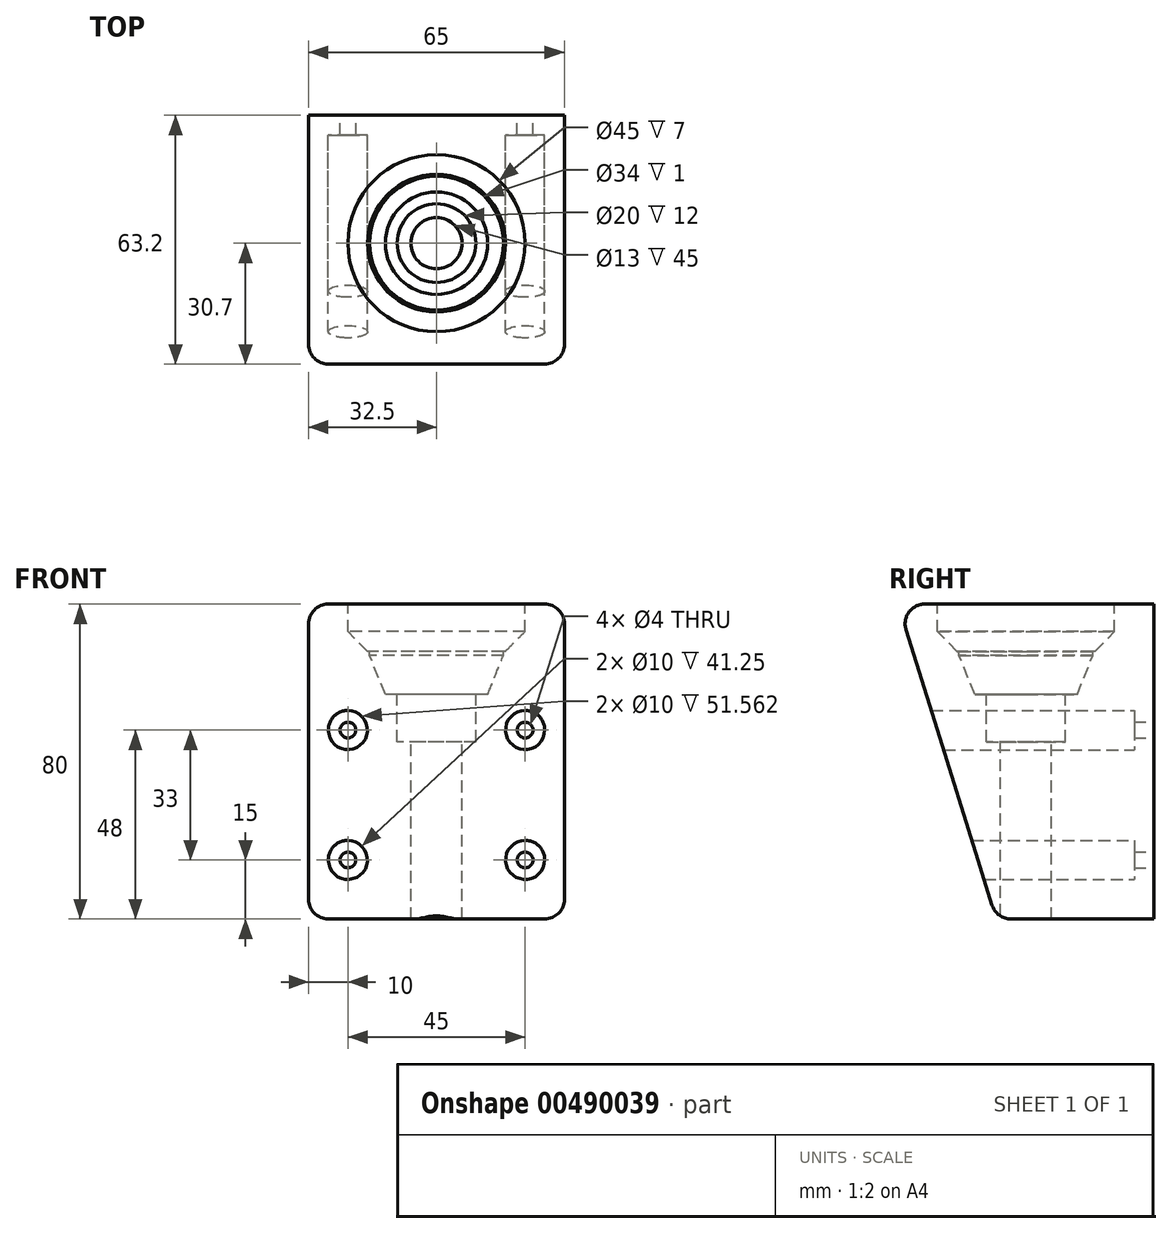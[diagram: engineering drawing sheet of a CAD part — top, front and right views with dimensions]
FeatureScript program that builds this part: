
annotation { "Feature Type Name" : "Feature", "Feature Type Description" : "" }
export const myFeature = defineFeature(function(context is Context, id is Id, definition is map)
    precondition{}
    {
        {
            var Q0;
            Q0=qCreatedBy(makeId("Right.planeOp"),FACE);
            var sketch = newSketch(context, id + "F0", { "sketchPlane" : qUnion([Q0])});
            skLineSegment(sketch, "E0", {"start": v(0, 0) * mm, "end": v(0, 80) * mm});
            skLineSegment(sketch, "E1", {"start": v(0, 80) * mm, "end": v(-65, 80) * mm});
            skLineSegment(sketch, "E2", {"start": v(0, 0) * mm, "end": v(-40, 0) * mm});
            skLineSegment(sketch, "E3", {"start": v(-40, 0) * mm, "end": v(-65, 80) * mm});
            skSolve(sketch);
        }
        {
            var Q0;
            Q0=makeQuery(id+"F0.imprint","IMPRINT",FACE,{"disambiguationData":[TD([[makeQuery(id+"F0.imprint","IMPRINT",EDGE,{"derivedFrom":sQuery(id+"F0.wireOp",EDGE,"E0")}),1.0]])]});
            extrude(context, id + "F1", {"entities" : qUnion([Q0]), "endBound" : BoundingType.SYMMETRIC, "depth" : 65 * mm});
        }
        {
            var Q0;
            Q0=makeQuery(id+"F1.opExtrude","SWEPT_FACE",FACE,{"disambiguationData":[OSD([sQuery(id+"F0.wireOp",EDGE,"E0")])]});
            var sketch = newSketch(context, id + "F2", { "sketchPlane" : qUnion([Q0])});
            skPoint(sketch, "E4", {"position": v(22.5, 15) * mm});
            skPoint(sketch, "E5", {"position": v(-22.5, 15) * mm});
            skPoint(sketch, "E6", {"position": v(-22.5, 48) * mm});
            skPoint(sketch, "E6.positionSnap0", {"position": v(22.5, 48) * mm});
            skSolve(sketch);
        }
        {
            var Q0;
            Q0=sQuery(id+"F2.wireOp",VERTEX,"E6");
            var Q1;
            Q1=sQuery(id+"F2.wireOp",VERTEX,"E6.positionSnap0");
            var Q2;
            Q2=sQuery(id+"F2.wireOp",VERTEX,"E4");
            var Q3;
            Q3=sQuery(id+"F2.wireOp",VERTEX,"E5");
            var Q4;
            Q4=makeQuery(id+"F1.opExtrude","SWEPT_BODY",BODY,{"disambiguationData":[OSD([sQuery(id+"F0.wireOp",EDGE,"E0"),sQuery(id+"F0.wireOp",EDGE,"E1"),sQuery(id+"F0.wireOp",EDGE,"E2"),sQuery(id+"F0.wireOp",EDGE,"E3")])]});
            hole(context, id + "F3", {"style" : HoleStyle.SIMPLE, "endStyle" : HoleEndStyle.THROUGH, "holeDiameter" : 4 * mm, "isTappedThrough" : true, "tappedDepth" : 12 * mm, "tapClearance" : 3, "locations" : qUnion([Q0, Q1, Q2, Q3]), "scope" : qUnion([Q4])});
        }
        {
            var Q0;
            Q0 = qBodyType(qCreatedBy(id + "F2" ,EDGE), BodyType.WIRE);
            var Q1;
            Q1=makeQuery(id+"F1.opExtrude","SWEPT_FACE",FACE,{"disambiguationData":[OSD([sQuery(id+"F0.wireOp",EDGE,"E0")])]});
            cPlane(context, id + "F4", {"entities" : qUnion([Q0, Q1]), "cplaneType" : CPlaneType.OFFSET, "offset" : 5 * mm, "oppositeDirection" : true, "width" : 150 * mm, "height" : 150 * mm});
        }
        {
            var Q0;
            Q0=qCreatedBy(id+"F4.planeOp",FACE);
            var sketch = newSketch(context, id + "F5", { "sketchPlane" : qUnion([Q0])});
            skCircle(sketch, "E7", {"center": v(-22.5, 48) * mm, "radius": 5 * mm});
            skCircle(sketch, "E8", {"center": v(-22.5, 15) * mm, "radius": 5 * mm});
            skCircle(sketch, "E9", {"center": v(22.5, 15) * mm, "radius": 5 * mm});
            skCircle(sketch, "E10", {"center": v(22.5, 48) * mm, "radius": 5 * mm});
            skSolve(sketch);
        }
        {
            var Q0;
            Q0 = qSketchRegion(id + "F5", true);
            extrude(context, id + "F6", {"entities" : qUnion([Q0]), "operationType" : NewBodyOperationType.REMOVE, "oppositeDirection" : true, "depth" : 60 * mm});
        }
        {
            var Q0;
            Q0=makeQuery(id+"F1.opExtrude","SWEPT_FACE",FACE,{"disambiguationData":[OSD([sQuery(id+"F0.wireOp",EDGE,"E1")])]});
            var sketch = newSketch(context, id + "F7", { "sketchPlane" : qUnion([Q0])});
            skPoint(sketch, "E11.endSnap0", {"position": v(0, 0) * mm});
            skPoint(sketch, "E12", {"position": v(0, -32.5) * mm});
            skCircle(sketch, "E13", {"center": v(0, -32.5) * mm, "radius": 22.5 * mm});
            skSolve(sketch);
        }
        {
            var Q0;
            Q0 = qSketchRegion(id + "F7", true);
            extrude(context, id + "F8", {"entities" : qUnion([Q0]), "operationType" : NewBodyOperationType.REMOVE, "oppositeDirection" : true, "depth" : 12 * mm});
        }
        {
            var Q0;
            Q0=makeQuery(id+"F8.boolean.opBoolean","COPY",FACE,{"derivedFrom":makeQuery(id+"F8.opExtrude","CAP_FACE",FACE,{"disambiguationData":[OSD([sQuery(id+"F7.wireOp",EDGE,"E13")])],"isStart":false})});
            var sketch = newSketch(context, id + "F9", { "sketchPlane" : qUnion([Q0])});
            skCircle(sketch, "E14", {"center": v(0, -32.5) * mm, "radius": 17 * mm});
            skSolve(sketch);
        }
        {
            var Q0;
            Q0=makeQuery(id+"F9.imprint","IMPRINT",FACE,{"disambiguationData":[TD([[makeQuery(id+"F9.imprint","IMPRINT",EDGE,{"derivedFrom":sQuery(id+"F9.wireOp",EDGE,"E14")}),1.0]])]});
            extrude(context, id + "F10", {"entities" : qUnion([Q0]), "operationType" : NewBodyOperationType.REMOVE, "oppositeDirection" : true, "depth" : 11 * mm});
        }
        {
            var Q0;
            Q0=makeQuery(id+"F10.boolean.opBoolean","COPY",FACE,{"derivedFrom":makeQuery(id+"F10.opExtrude","CAP_FACE",FACE,{"disambiguationData":[OSD([sQuery(id+"F9.wireOp",EDGE,"E14")])],"isStart":false})});
            var sketch = newSketch(context, id + "F11", { "sketchPlane" : qUnion([Q0])});
            skCircle(sketch, "E15", {"center": v(0, -32.5) * mm, "radius": 10 * mm});
            skSolve(sketch);
        }
        {
            var Q0;
            Q0 = qSketchRegion(id + "F11", true);
            extrude(context, id + "F12", {"entities" : qUnion([Q0]), "operationType" : NewBodyOperationType.REMOVE, "oppositeDirection" : true, "depth" : 12 * mm});
        }
        {
            var Q0;
            Q0=makeQuery(id+"F11.imprint","IMPRINT",FACE,{"disambiguationData":[TD([[makeQuery(id+"F11.imprint","IMPRINT",EDGE,{"derivedFrom":sQuery(id+"F11.wireOp",EDGE,"E15")}),1.0]])]});
            var sketch = newSketch(context, id + "F13", { "sketchPlane" : qUnion([Q0])});
            skCircle(sketch, "E16", {"center": v(0, -32.5) * mm, "radius": 6.5 * mm});
            skSolve(sketch);
        }
        {
            var Q0;
            Q0 = qSketchRegion(id + "F13", true);
            extrude(context, id + "F14", {"entities" : qUnion([Q0]), "operationType" : NewBodyOperationType.REMOVE, "oppositeDirection" : true, "depth" : 80 * mm});
        }
        {
            var Q0;
            Q0=makeQuery(id+"F8.boolean.opBoolean","COPY",EDGE,{"derivedFrom":makeQuery(id+"F8.opExtrude","CAP_EDGE",EDGE,{"disambiguationData":[OSD([sQuery(id+"F7.wireOp",EDGE,"E13")])],"isStart":false})});
            chamfer(context, id + "F15", {"entities" : qUnion([Q0]), "chamferType" : ChamferType.TWO_OFFSETS, "width1" : 5 * mm, "oppositeDirection" : false, "width2" : 5 * mm, "tangentPropagation" : true});
        }
        {
            var Q0;
            Q0=makeQuery(id+"F10.boolean.opBoolean","COPY",EDGE,{"derivedFrom":makeQuery(id+"F10.opExtrude","CAP_EDGE",EDGE,{"disambiguationData":[OSD([sQuery(id+"F9.wireOp",EDGE,"E14")])],"isStart":false})});
            chamfer(context, id + "F16", {"entities" : qUnion([Q0]), "chamferType" : ChamferType.TWO_OFFSETS, "width1" : 4 * mm, "oppositeDirection" : false, "width2" : 10 * mm, "tangentPropagation" : true});
        }
        {
            var Q0;
            Q0=makeQuery(id+"F1.opExtrude","CAP_EDGE",EDGE,{"disambiguationData":[OSD([sQuery(id+"F0.wireOp",EDGE,"E1")])],"isStart":true});
            var Q1;
            Q1=makeQuery(id+"F1.opExtrude","SWEPT_EDGE",EDGE,{"disambiguationData":[OSD([sQuery(id+"F0.wireOp",EDGE,"E1"),sQuery(id+"F0.wireOp",EDGE,"E3")])]});
            var Q2;
            Q2=makeQuery(id+"F1.opExtrude","CAP_EDGE",EDGE,{"disambiguationData":[OSD([sQuery(id+"F0.wireOp",EDGE,"E1")])],"isStart":false});
            var Q3;
            Q3=makeQuery(id+"F1.opExtrude","CAP_EDGE",EDGE,{"disambiguationData":[OSD([sQuery(id+"F0.wireOp",EDGE,"E3")])],"isStart":false});
            var Q4;
            Q4=makeQuery(id+"F1.opExtrude","CAP_EDGE",EDGE,{"disambiguationData":[OSD([sQuery(id+"F0.wireOp",EDGE,"E3")])],"isStart":true});
            var Q5;
            Q5=makeQuery(id+"F1.opExtrude","SWEPT_EDGE",EDGE,{"disambiguationData":[OSD([sQuery(id+"F0.wireOp",EDGE,"E2"),sQuery(id+"F0.wireOp",EDGE,"E3")])]});
            var Q6;
            Q6=makeQuery(id+"F1.opExtrude","CAP_EDGE",EDGE,{"disambiguationData":[OSD([sQuery(id+"F0.wireOp",EDGE,"E2")])],"isStart":false});
            var Q7;
            Q7=makeQuery(id+"F1.opExtrude","CAP_EDGE",EDGE,{"disambiguationData":[OSD([sQuery(id+"F0.wireOp",EDGE,"E2")])],"isStart":true});
            fillet(context, id + "F17", {"entities" : qUnion([Q0, Q1, Q2, Q3, Q4, Q5, Q6, Q7]), "radius" : 5 * mm, "tangentPropagation" : true, "allowEdgeOverflow" : false});
        }
    });
